# Revit family: CENTUM Unterlegteil AF
name_source: partatom
category: HLS-Bauteile
revit_build: Autodesk Revit 2017 (Build: 20190507_1515(x64)
units: mm (PartAtom-declared; Revit-internal decimal feet)

## family parameters
Arbeitsebenenbasiert = Ja
Beim Laden mit Abzugskörper schneiden = Nein
Bemaßung runder Anschluss = Durchmesser verwenden
Gemeinsam genutzt = Ja
Immer vertikal = Nein
Raumberechnungspunkt = Nein
Teiletyp = Normal

## types (6) — shared parameters
Fabrikat = MEFA
Firma = MEFA Befestigungs- und Montagesysteme GmbH
Kurztext1 = Unterlegteil CENTUM Spannklaue AF
Material = Stahl
Mengeneinheit = St
Oberflaeche = feuerstückverzinkt
Vorgabe-Ansicht = 1219 mm
vpe = 1 St

## per-type parameters (varying)
| type | Artikelnummer | B1 | B2 | Breite | D | EAN | Gewicht | Gewicht pro Bauteil | Kurztext2 | L1 | Länge | Nockenhöhe Spannklaue | Stärke | T | Typ | für Gewinde |
| CENTUM Unterlegteil AF 12 CW, M12 | 0576012 | 40 mm  [stored 0.131234 ft] | 40 mm  [stored 0.131234 ft] | 40 mm  [stored 0.131234 ft] | 19 mm  [stored 0.062336 ft] | 4250928414519 | 0.03 kg | 0.03 kg | Typ 12 CW Stärke 2 mm für AF M12 | 7 mm  [stored 0.0229659 ft] | 40 mm  [stored 0.131234 ft] | 7 mm | 2 mm  [stored 0.00656168 ft] | 2 mm  [stored 0.00656168 ft] | 12 CW | M12 |
| CENTUM Unterlegteil AF 12 P1, M12 | 0576082 | 40 mm  [stored 0.131234 ft] | 40 mm  [stored 0.131234 ft] | 40 mm  [stored 0.131234 ft] | 19 mm  [stored 0.062336 ft] | 4250928414533 | 0.07 kg | 0.07 kg | Typ 12 P1 Stärke 5 mm für AF M12 | 7 mm  [stored 0.0229659 ft] | 40 mm  [stored 0.131234 ft] | 7 mm | 5 mm  [stored 0.0164042 ft] | 5 mm  [stored 0.0164042 ft] | 12 P1 | M12 |
| CENTUM Unterlegteil AF 12 P2, M12 | 0576112 | 40 mm  [stored 0.131234 ft] | 40 mm  [stored 0.131234 ft] | 40 mm  [stored 0.131234 ft] | 19 mm  [stored 0.062336 ft] | 4250928414540 | 0.12 kg | 0.12 kg | Typ 12 P2 Stärke 10 mm für AF M12 | 7 mm  [stored 0.0229659 ft] | 40 mm  [stored 0.131234 ft] | 7 mm | 10 mm  [stored 0.0328084 ft] | 10 mm  [stored 0.0328084 ft] | 12 P2 | M12 |
| CENTUM Unterlegteil AF 16 CW, M16 | 0576016 | 48 mm  [stored 0.15748 ft] | 50 mm  [stored 0.164042 ft] | 50 mm  [stored 0.164042 ft] | 24 mm  [stored 0.0787402 ft] | 4250928414526 | 0.04 kg | 0.04 kg | Typ 16 CW Stärke 2 mm für AF M16 | 8 mm  [stored 0.0262467 ft] | 48 mm  [stored 0.15748 ft] | 8 mm | 2 mm  [stored 0.00656168 ft] | 2 mm  [stored 0.00656168 ft] | 16 CW | M16 |
| CENTUM Unterlegteil AF 16 P1, M16 | 0576114 | 50 mm  [stored 0.164042 ft] | 52 mm | 52 mm | 23 mm  [stored 0.0754593 ft] | 4250928414557 | 0.10 kg | 0.10 kg | Typ 16 P1 Stärke 5 mm für AF M16 | 8 mm  [stored 0.0262467 ft] | 50 mm  [stored 0.164042 ft] | 8 mm | 5 mm  [stored 0.0164042 ft] | 5 mm  [stored 0.0164042 ft] | 16 P1 | M16 |
| CENTUM Unterlegteil AF 16 P2, M16 | 0576116 | 50 mm  [stored 0.164042 ft] | 52 mm | 52 mm | 23 mm  [stored 0.0754593 ft] | 4250928414564 | 0.20 kg | 0.20 kg | Typ 16 P2 Stärke 10 mm für AF M16 | 8 mm  [stored 0.0262467 ft] | 50 mm  [stored 0.164042 ft] | 8 mm | 10 mm  [stored 0.0328084 ft] | 10 mm  [stored 0.0328084 ft] | 16 P2 | M16 |

note: [stored X ft] marks values corroborated as IEEE doubles in the binary element streams (Revit-internal decimal feet)
